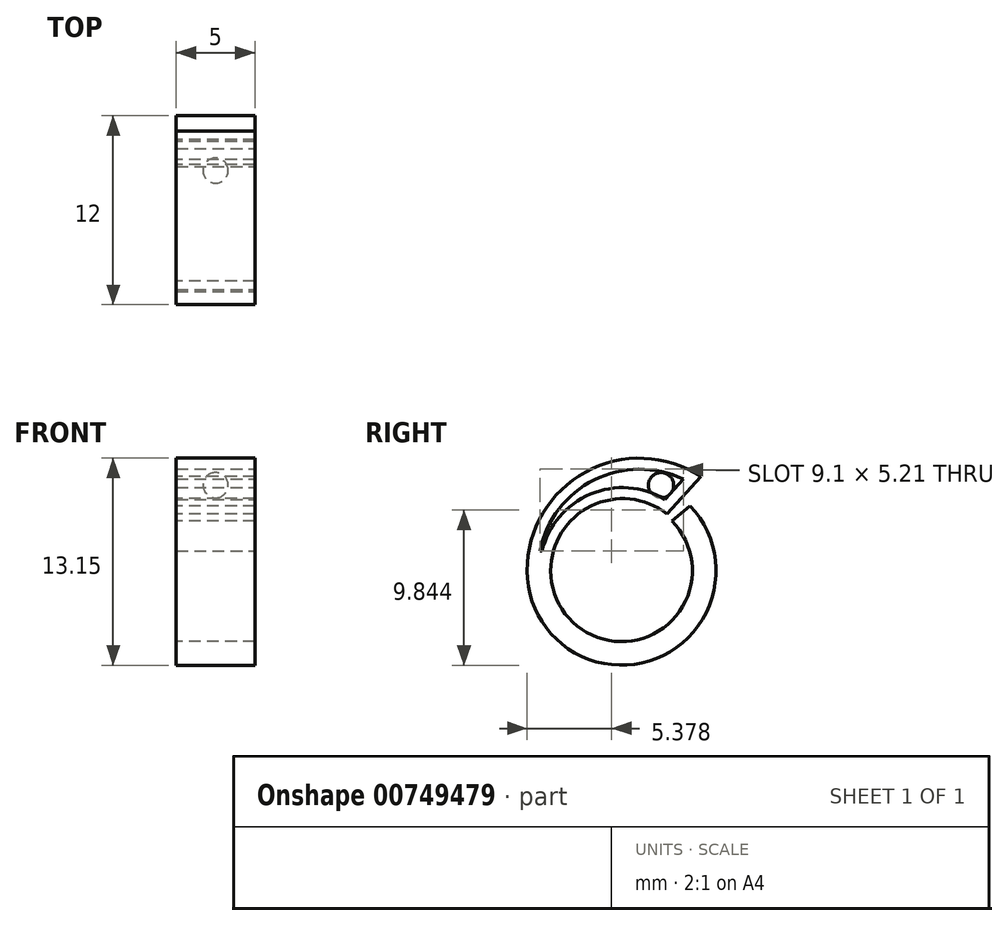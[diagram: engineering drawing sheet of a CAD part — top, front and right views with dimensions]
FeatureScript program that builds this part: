
annotation { "Feature Type Name" : "Feature", "Feature Type Description" : "" }
export const myFeature = defineFeature(function(context is Context, id is Id, definition is map)
    precondition{}
    {
        {
            var Q0;
            Q0=qCreatedBy(makeId("Right.planeOp"),FACE);
            var sketch = newSketch(context, id + "F0", { "sketchPlane" : qUnion([Q0])});
            skArc(sketch, "E0", {"start": v(-4.5, 0) * mm, "mid": v(1.7, -4.16) * mm, "end": v(3.2, 3.16) * mm});
            skArc(sketch, "E1.0", {"start": v(-6, 0) * mm, "mid": v(2.22, -5.57) * mm, "end": v(4.36, 4.12) * mm});
            skLineSegment(sketch, "E2", {"start": v(3.2, 3.16) * mm, "end": v(4.36, 4.12) * mm});
            skLineSegment(sketch, "E3", {"start": v(-6, 0) * mm, "end": v(-6, -10.6) * mm, "construction": true});
            skLineSegment(sketch, "E4", {"start": v(-4.5, 0) * mm, "end": v(-4.5, -8.26) * mm, "construction": true});
            skArc(sketch, "E5", {"start": v(5.03, 6) * mm, "mid": v(-2.27, 6.28) * mm, "end": v(-6, 0) * mm});
            skArc(sketch, "E6", {"start": v(2.89, 3.61) * mm, "mid": v(-1.93, 4.11) * mm, "end": v(-4.5, 0) * mm});
            skLineSegment(sketch, "E7", {"start": v(5.03, 6) * mm, "end": v(2.89, 3.61) * mm});
            skSolve(sketch);
        }
        {
            var Q0;
            Q0 = qSketchRegion(id + "F0", true);
            extrude(context, id + "F1", {"entities" : qUnion([Q0]), "endBound" : BoundingType.SYMMETRIC, "depth" : 5 * mm, "offsetDistance" : 25 * mm});
        }
        {
            var Q0;
            Q0=makeQuery(id+"F1.opExtrude","CAP_FACE",FACE,{"disambiguationData":[OSD([sQuery(id+"F0.wireOp",EDGE,"E0"),sQuery(id+"F0.wireOp",EDGE,"E1.0"),sQuery(id+"F0.wireOp",EDGE,"E2"),sQuery(id+"F0.wireOp",EDGE,"E5"),sQuery(id+"F0.wireOp",EDGE,"E6"),sQuery(id+"F0.wireOp",EDGE,"E7")])],"isStart":false});
            var sketch = newSketch(context, id + "F2", { "sketchPlane" : qUnion([Q0])});
            skSolve(sketch);
        }
        {
            var Q0;
            Q0=makeQuery(id+"F2.imprint","IMPRINT",FACE,{"disambiguationData":[TD([[makeQuery(id+"F2.imprint","IMPRINT",EDGE,{"derivedFrom":makeQuery(id+"F1.opExtrude","CAP_EDGE",EDGE,{"disambiguationData":[OSD([sQuery(id+"F0.wireOp",EDGE,"E0")])],"isStart":false})}),-1.0]])]});
            var sketch = newSketch(context, id + "F3", { "sketchPlane" : qUnion([Q0])});
            skArc(sketch, "E8.0", {"start": v(3.93, 5.82) * mm, "mid": v(-1.73, 5.77) * mm, "end": v(-5.17, 1.27) * mm});
            skLineSegment(sketch, "E8.1", {"start": v(3.93, 5.82) * mm, "end": v(2.78, 4.53) * mm});
            skArc(sketch, "E8.2", {"start": v(2.78, 4.53) * mm, "mid": v(-1.97, 4.86) * mm, "end": v(-5.05, 1.24) * mm});
            skLineSegment(sketch, "E9", {"start": v(-5.17, 1.27) * mm, "end": v(-5.05, 1.24) * mm});
            skSolve(sketch);
        }
        {
            var Q0;
            Q0 = qSketchRegion(id + "F3", true);
            extrude(context, id + "F4", {"entities" : qUnion([Q0]), "operationType" : NewBodyOperationType.REMOVE, "oppositeDirection" : true, "depth" : 25 * mm, "offsetDistance" : 25 * mm});
        }
        {
            var Q0;
            Q0=qCreatedBy(makeId("Right.planeOp"),FACE);
            var sketch = newSketch(context, id + "F5", { "sketchPlane" : qUnion([Q0])});
            skArc(sketch, "E10", {"start": v(2.51, 4.63) * mm, "mid": v(3.32, 5.43) * mm, "end": v(2.51, 6.24) * mm});
            skLineSegment(sketch, "E11", {"start": v(2.51, 6.24) * mm, "end": v(2.51, 4.63) * mm});
            skSolve(sketch);
        }
        {
            var Q0;
            Q0 = qSketchRegion(id + "F5", true);
            var Q1;
            Q1=sQuery(id+"F5.wireOp",EDGE,"E11");
            revolve(context, id + "F6", {"surfaceOperationType" : NewSurfaceOperationType.NEW, "entities" : qUnion([Q0]), "axis" : qUnion([Q1]), "revolveType" : RevolveType.FULL});
        }
    });
